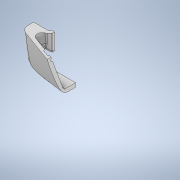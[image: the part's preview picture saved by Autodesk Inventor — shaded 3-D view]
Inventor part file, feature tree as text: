
AUTODESK INVENTOR PART (.ipt)
format: ipt  version: 2022 (Build 260153000, 153)  size: 2,179,072 bytes
history: native  units: mm
features: sketch x18, reference x18, other x13, extrude x12, fillet x11, projected_geometry x9, chamfer x3, loft x1, revolve x1, mirror x1
ambient origin geometry x8: Origin, YZ Plane, XZ Plane, XY Plane, X Axis, Y Axis, Z Axis, Center Point
bodies: Body1 (feature_tree)
feature tree (87):
  other  "Твердое тело1"
  other  "РабТочка1"
  extrude  "Выдавливание1"  Depth=30.0mm TaperAngle=0.0deg
  extrude  "Выдавливание2"  Depth=60.0mm TaperAngle=0.0deg
  sketch  "Эскиз4"
  sketch  "Эскиз5"
  sketch  "Эскиз6"
  extrude  "Выдавливание4"  Depth=0.25mm
  sketch  "Эскиз8"
  other  "РабПлоскость1"
  loft  "Лофт8"
  fillet  "Сопряжение5"  Radius=0.2mm
  extrude  "Выдавливание5"  Depth=0.5mm
  revolve  "Вращение1"
  fillet  "Сопряжение6"  Radius=2.0mm
  fillet  "Сопряжение7"  Radius=8.0mm
  other  "РабПлоскость2"
  sketch  "Эскиз13"
  extrude  "Выдавливание6"  Depth=2.0mm
  extrude  "Выдавливание7"  Depth=4.0mm
  fillet  "Сопряжение8"  Radius=4.0mm
  extrude  "Выдавливание8"  Depth=15.0mm TaperAngle=0.0deg
  fillet  "Сопряжение9"  [1 undecoded]
  extrude  "Выдавливание9"  Depth=4.0mm
  fillet  "Сопряжение10"  Radius=6.0mm
  fillet  "Сопряжение11"  Radius=0.3mm
  extrude  "Выдавливание10"  Depth=10.0mm TaperAngle=0.0deg
  extrude  "Выдавливание11"  Depth=3.0mm TaperAngle=0.0deg
  chamfer  "Фаска1"  Distance=2.0mm
  chamfer  "Фаска2"  Distance=5.0mm
  fillet  "Сопряжение12"  Radius=9.0mm
  fillet  "Сопряжение13"  Radius=11.0mm
  fillet  "Сопряжение14"  Radius=1.5mm
  fillet  "Сопряжение15"  Radius=4.0mm
  sketch  "Эскиз19"
  other  "РабПлоскость3"
  extrude  "Выдавливание12"  Depth=0.75mm
  chamfer  "Фаска3"  Distance=0.8mm
  mirror  "Зеркальное отражение1"
  extrude  "Выдавливание13"  Depth=0.8mm
  sketch  "Эскиз1"
  reference  "Ссылка1"
  reference  "Ссылка2"
  reference  "Ссылка3"
  reference  "Ссылка4"
  sketch  "Эскиз2"
  reference  "Ссылка5"
  projected_geometry  "Спроецированная петля1"
  reference  "Ссылка6"
  reference  "Ссылка11"
  reference  "Ссылка13"
  sketch  "Эскиз7"
  reference  "Ссылка15"
  reference  "Ссылка16"
  reference  "Ссылка17"
  reference  "Ссылка18"
  reference  "Ссылка19"
  projected_geometry  "Спроецированная петля13"
  reference  "Ссылка22"
  sketch  "Эскиз9"
  projected_geometry  "Спроецированная петля14"
  sketch  "Эскиз11"
  sketch  "Эскиз12"
  projected_geometry  "Спроецированная петля18"
  reference  "Ссылка23"
  sketch  "Эскиз14"
  sketch  "Эскиз15"
  reference  "Ссылка24"
  sketch  "Эскиз16"
  projected_geometry  "Спроецированная петля19"
  projected_geometry  "Спроецированная петля20"
  sketch  "Эскиз17"
  reference  "Ссылка25"
  projected_geometry  "Спроецированная петля21"
  sketch  "Эскиз18"
  projected_geometry  "Спроецированная петля22"
  reference  "Ссылка26"
  projected_geometry  "Спроецированная петля23"
  sketch  "Эскиз20"
  other  "<userpath>\Documents\Git\MZCAT_2024\MZCAT_4.iam"
  other  "MZCAT_4.iam"
  other  "back_diffuser:1"
  other  "CAT_protector:1"
  other  "magazine_fixator:1"
  other  "vydacha_slide:1"
  other  "back_led_board:1"
  other  "antenna:2"
note: 1 required parameter value undecoded (feature->parameter linkage not recoverable at this tier; creation-order binding heuristic only, values carry confidence <= 0.55)
